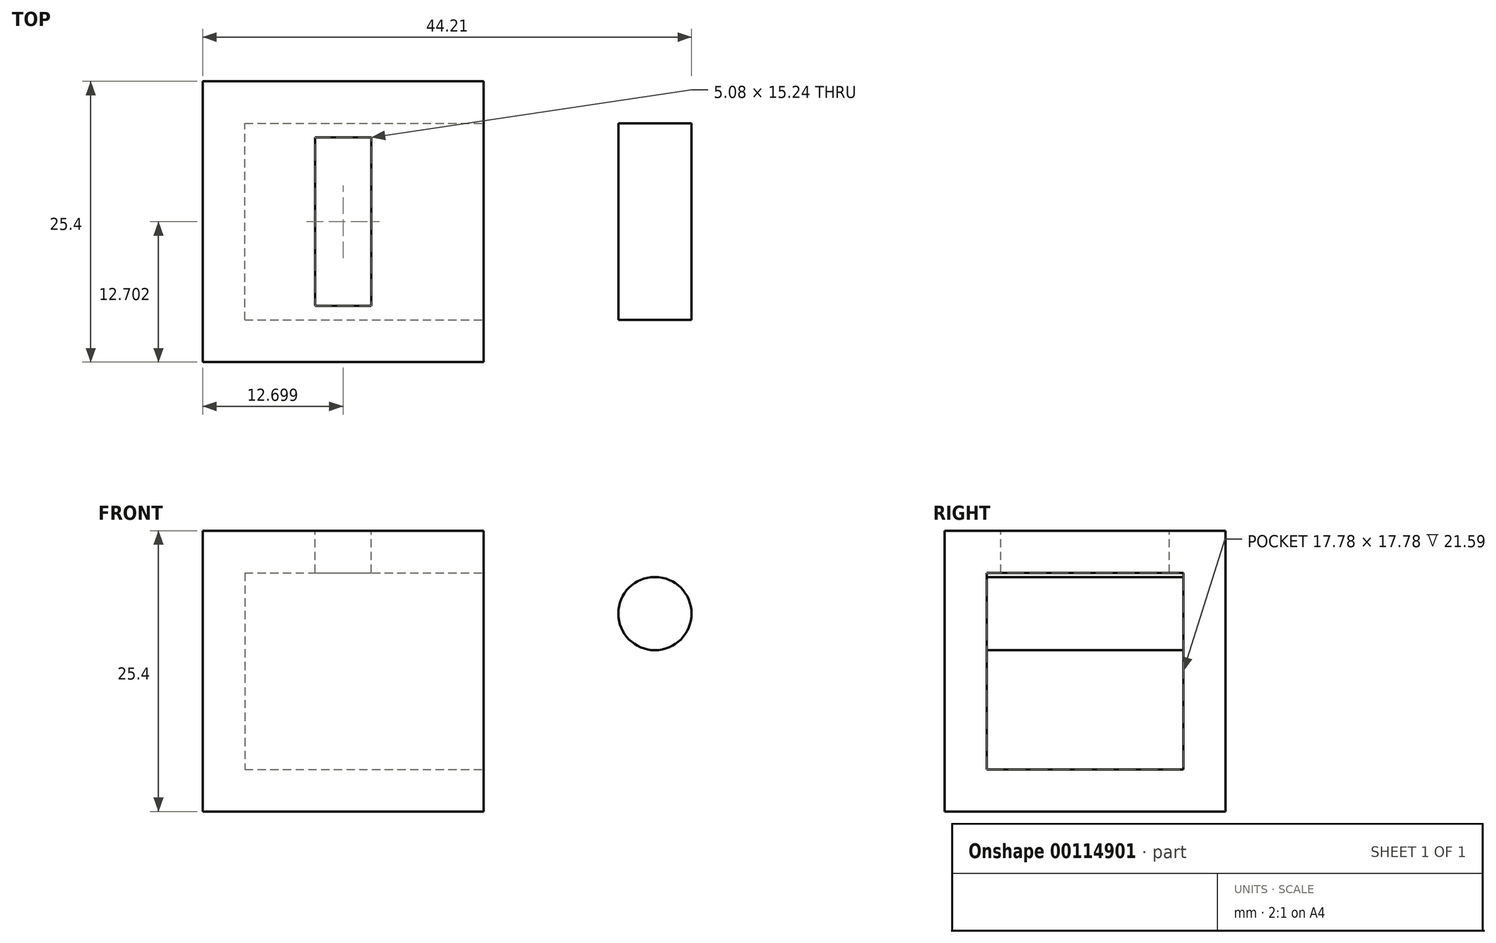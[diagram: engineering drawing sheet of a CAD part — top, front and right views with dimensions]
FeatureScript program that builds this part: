
annotation { "Feature Type Name" : "Feature", "Feature Type Description" : "" }
export const myFeature = defineFeature(function(context is Context, id is Id, definition is map)
    precondition{}
    {
        {
            var Q0;
            Q0=qCreatedBy(makeId("Top.planeOp"),FACE);
            var sketch = newSketch(context, id + "F0", { "sketchPlane" : qUnion([Q0])});
            skLineSegment(sketch, "E0.bottom", {"start": v(-4.98, -4.4) * mm, "end": v(20.42, -4.4) * mm});
            skLineSegment(sketch, "E0.top", {"start": v(-4.98, 21) * mm, "end": v(20.42, 21) * mm});
            skLineSegment(sketch, "E0.left", {"start": v(-4.98, -4.4) * mm, "end": v(-4.98, 21) * mm});
            skLineSegment(sketch, "E0.right", {"start": v(20.42, -4.4) * mm, "end": v(20.42, 21) * mm});
            skSolve(sketch);
        }
        {
            var Q0;
            Q0=makeQuery(id+"F0.imprint","IMPRINT",FACE,{"disambiguationData":[TD([[makeQuery(id+"F0.imprint","IMPRINT",EDGE,{"derivedFrom":sQuery(id+"F0.wireOp",EDGE,"E0.bottom")}),1.0]])]});
            extrude(context, id + "F1", {"entities" : qUnion([Q0]), "depth" : 25.4 * mm});
        }
        {
            var Q0;
            Q0=makeQuery(id+"F1.opExtrude","CAP_FACE",FACE,{"disambiguationData":[OSD([sQuery(id+"F0.wireOp",EDGE,"E0.bottom"),sQuery(id+"F0.wireOp",EDGE,"E0.top"),sQuery(id+"F0.wireOp",EDGE,"E0.left"),sQuery(id+"F0.wireOp",EDGE,"E0.right")])],"isStart":false});
            var sketch = newSketch(context, id + "F2", { "sketchPlane" : qUnion([Q0])});
            skLineSegment(sketch, "E1.bottom", {"start": v(5.18, 15.92) * mm, "end": v(10.26, 15.92) * mm});
            skLineSegment(sketch, "E1.top", {"start": v(5.18, 0.68) * mm, "end": v(10.26, 0.68) * mm});
            skLineSegment(sketch, "E1.left", {"start": v(5.18, 15.92) * mm, "end": v(5.18, 0.68) * mm});
            skLineSegment(sketch, "E1.right", {"start": v(10.26, 15.92) * mm, "end": v(10.26, 0.68) * mm});
            skSolve(sketch);
        }
        {
            var Q0;
            Q0=makeQuery(id+"F1.opExtrude","SWEPT_FACE",FACE,{"disambiguationData":[OSD([sQuery(id+"F0.wireOp",EDGE,"E0.right")])]});
            shell(context, id + "F3", {"entities" : qUnion([Q0]), "thickness" : 3.8 * mm});
        }
        {
            var Q0;
            Q0=makeQuery(id+"F2.imprint","IMPRINT",FACE,{"disambiguationData":[TD([[makeQuery(id+"F2.imprint","IMPRINT",EDGE,{"derivedFrom":sQuery(id+"F2.wireOp",EDGE,"E1.bottom")}),-1.0]])]});
            extrude(context, id + "F4", {"entities" : qUnion([Q0]), "operationType" : NewBodyOperationType.REMOVE, "oppositeDirection" : true, "depth" : 3.8 * mm});
        }
        {
            var Q0;
            Q0=makeQuery(id+"F3.opShell","OFFSET_FACE",FACE,{"disambiguationData":[OSD([sQuery(id+"F0.wireOp",EDGE,"E0.top")])]});
            var sketch = newSketch(context, id + "F5", { "sketchPlane" : qUnion([Q0])});
            skCircle(sketch, "E2", {"center": v(35.92, 17.9) * mm, "radius": 3.31 * mm});
            skSolve(sketch);
        }
        {
            var Q0;
            Q0=qSketchRegion(id+"F5",true);
            extrude(context, id + "F6", {"entities" : qUnion([Q0]), "depth" : 17.78 * mm});
        }
    });
